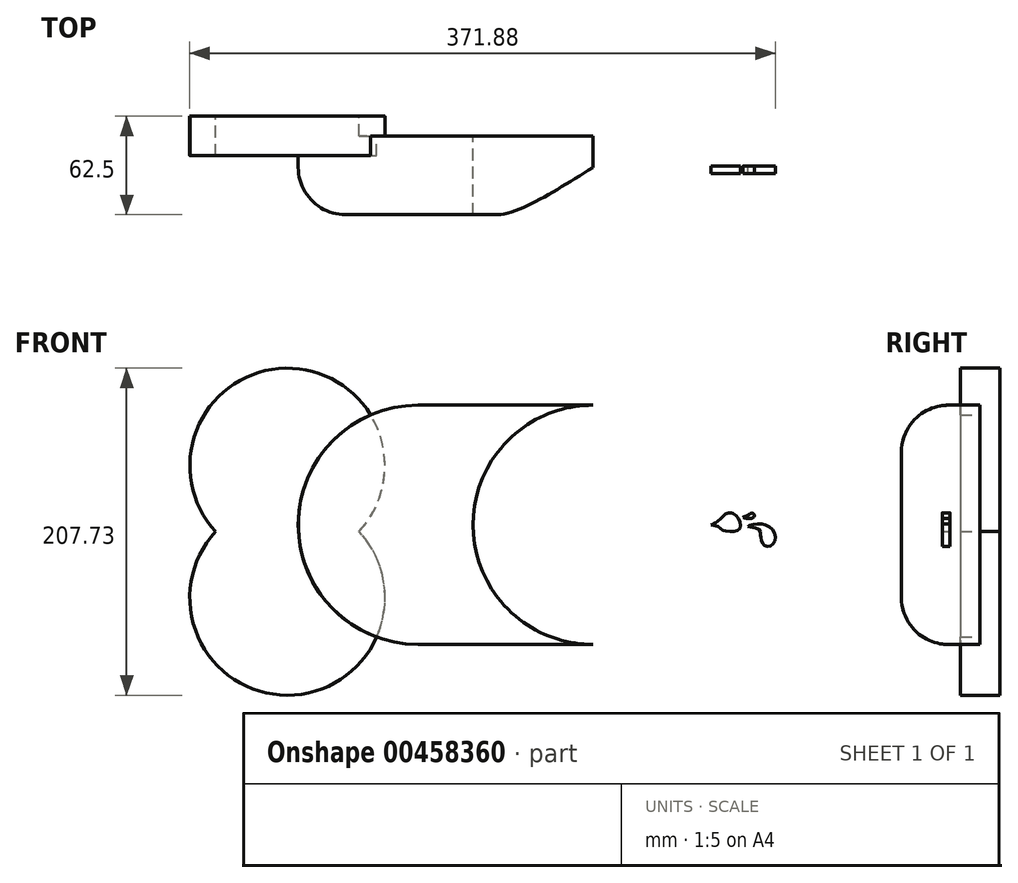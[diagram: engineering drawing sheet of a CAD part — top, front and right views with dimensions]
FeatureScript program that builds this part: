
annotation { "Feature Type Name" : "Feature", "Feature Type Description" : "" }
export const myFeature = defineFeature(function(context is Context, id is Id, definition is map)
    precondition{}
    {
        {
            var Q0;
            Q0=qCreatedBy(makeId("Front.planeOp"),FACE);
            var sketch = newSketch(context, id + "F0", { "sketchPlane" : qUnion([Q0])});
            skCircle(sketch, "E0", {"center": v(0, 0) * mm, "radius": 76 * mm});
            skCircle(sketch, "E1", {"center": v(111, 0) * mm, "radius": 76 * mm});
            skLineSegment(sketch, "E2", {"start": v(111, 76) * mm, "end": v(0, 76) * mm});
            skLineSegment(sketch, "E3", {"start": v(0, -76) * mm, "end": v(111, -76) * mm});
            skSolve(sketch);
        }
        {
            var Q0;
            Q0=qCreatedBy(makeId("Front.planeOp"),FACE);
            cPlane(context, id + "F1", {"entities" : qUnion([Q0]), "cplaneType" : CPlaneType.OFFSET, "offset" : 19 * mm, "width" : 150 * mm, "height" : 150 * mm});
        }
        {
            var Q0;
            {var subQ0=sQuery(id+"F0.wireOp",EDGE,"E0");var subQ1=makeQuery(id+"F0.imprint","INTERSECT",VERTEX,{"derivedFrom":[subQ0,sQuery(id+"F0.wireOp",EDGE,"E2")]});Q0=makeQuery(id+"F0.imprint","IMPRINT",FACE,{"disambiguationData":[TD([[makeQuery(id+"F0.imprint","IMPRINT",EDGE,{"disambiguationData":[TD([[subQ1,1.0]])],"derivedFrom":subQ0}),1.0]])]});}
            var Q1;
            {var subQ0=sQuery(id+"F0.wireOp",EDGE,"E1");var subQ1=sQuery(id+"F0.wireOp",EDGE,"E0");var subQ2=makeQuery(id+"F0.imprint","INTERSECT",VERTEX,{"disambiguationData":[OD(0.0)],"derivedFrom":[subQ1,subQ0]});Q1=makeQuery(id+"F0.imprint","IMPRINT",FACE,{"disambiguationData":[TD([[makeQuery(id+"F0.imprint","IMPRINT",EDGE,{"disambiguationData":[TD([[subQ2,1.0]])],"derivedFrom":subQ1}),-1.0]])]});}
            var Q2;
            {var subQ0=sQuery(id+"F0.wireOp",EDGE,"E1");var subQ1=sQuery(id+"F0.wireOp",EDGE,"E0");var subQ2=makeQuery(id+"F0.imprint","INTERSECT",VERTEX,{"disambiguationData":[OD(0.0)],"derivedFrom":[subQ1,subQ0]});Q2=makeQuery(id+"F0.imprint","IMPRINT",FACE,{"disambiguationData":[TD([[makeQuery(id+"F0.imprint","IMPRINT",EDGE,{"disambiguationData":[TD([[subQ2,1.0]])],"derivedFrom":subQ1}),1.0]])]});}
            var Q3;
            {var subQ0=sQuery(id+"F0.wireOp",EDGE,"E3");Q3=makeQuery(id+"F0.imprint","IMPRINT",FACE,{"disambiguationData":[TD([[makeQuery(id+"F0.imprint","IMPRINT",EDGE,{"derivedFrom":subQ0}),1.0]])]});}
            var Q4;
            {var subQ0=sQuery(id+"F0.wireOp",EDGE,"E2");Q4=makeQuery(id+"F0.imprint","IMPRINT",FACE,{"disambiguationData":[TD([[makeQuery(id+"F0.imprint","IMPRINT",EDGE,{"derivedFrom":subQ0}),1.0]])]});}
            extrude(context, id + "F2", {"entities" : qUnion([Q0, Q1, Q2, Q3, Q4]), "depth" : 50 * mm, "offsetDistance" : 25 * mm});
        }
        {
            var Q0;
            Q0=qCreatedBy(makeId("Front.planeOp"),FACE);
            var sketch = newSketch(context, id + "F3", { "sketchPlane" : qUnion([Q0])});
            skCircle(sketch, "E4", {"center": v(-82.93, 37.57) * mm, "radius": 61.92 * mm});
            skCircle(sketch, "E5", {"center": v(-82.93, -46.23) * mm, "radius": 62 * mm});
            skSolve(sketch);
        }
        {
            var Q0;
            Q0 = qSketchRegion(id + "F3", true);
            extrude(context, id + "F4", {"entities" : qUnion([Q0]), "operationType" : NewBodyOperationType.ADD, "depth" : 25 * mm, "offsetDistance" : 25 * mm, "symmetric" : true});
        }
        {
            var Q0;
            Q0=makeQuery(id+"F2.opExtrude","CAP_EDGE",EDGE,{"disambiguationData":[OSD([sQuery(id+"F0.wireOp",EDGE,"E0")])],"isStart":false});
            fillet(context, id + "F5", {"entities" : qUnion([Q0]), "radius" : 30 * mm, "tangentPropagation" : true, "allowEdgeOverflow" : false});
        }
        {
            var Q0;
            Q0=makeQuery(id+"F2.opExtrude","CAP_FACE",FACE,{"disambiguationData":[OSD([sQuery(id+"F0.wireOp",EDGE,"E0"),sQuery(id+"F0.wireOp",EDGE,"E1"),sQuery(id+"F0.wireOp",EDGE,"E2"),sQuery(id+"F0.wireOp",EDGE,"E3")])],"isStart":false});
            var sketch = newSketch(context, id + "F6", { "sketchPlane" : qUnion([Q0])});
            skLineSegment(sketch, "E6.bottom", {"start": v(187.67, -0.36) * mm, "end": v(169.29, -0.36) * mm});
            skLineSegment(sketch, "E6.top", {"start": v(187.67, 0.36) * mm, "end": v(169.29, 0.36) * mm});
            skLineSegment(sketch, "E6.left", {"start": v(187.67, -0.36) * mm, "end": v(187.67, 0.36) * mm});
            skLineSegment(sketch, "E6.right", {"start": v(169.29, -0.36) * mm, "end": v(169.29, 0.36) * mm});
            skPoint(sketch, "E6.middle", {"position": v(178.48, 0) * mm});
            skPoint(sketch, "E6.middle.positionSnap0", {"position": v(157, 0) * mm});
            skPoint(sketch, "E6.centerSnap0", {"position": v(157, 0) * mm});
            skSolve(sketch);
        }
        {
            var Q0;
            Q0 = qSketchRegion(id + "F6", true);
            extrude(context, id + "F7", {"entities" : qUnion([Q0]), "operationType" : NewBodyOperationType.REMOVE, "endBound" : BoundingType.THROUGH_ALL, "oppositeDirection" : true, "depth" : 25 * mm, "offsetDistance" : 25 * mm});
        }
        {
            var Q0;
            Q0=qCreatedBy(id+"F1.planeOp",FACE);
            var sketch = newSketch(context, id + "F8", { "sketchPlane" : qUnion([Q0])});
            skFitSpline(sketch, "E7", {"points": [v(186.24, 0) * mm, v(187.8, 0.43) * mm, v(189.84, 2.04) * mm, v(193, 4.3) * mm, v(195.65, 7.27) * mm, v(199.16, 7.5) * mm, v(199.48, 7.34) * mm, v(202.19, 5.7) * mm, v(204.6, 1.1) * mm, v(204.5, -2.17) * mm, v(201.72, -4.07) * mm, v(196.13, -4.1) * mm, v(193.03, -3.17) * mm, v(190.25, -0.88) * mm, v(186.24, 0) * mm]});
            skFitSpline(sketch, "E8", {"points": [v(209.6, -1.15) * mm, v(213.6, 0.4) * mm, v(220.46, 0) * mm, v(225.93, -4.06) * mm, v(226.45, -10.8) * mm, v(223.05, -13.73) * mm, v(219.27, -12.22) * mm, v(217.87, -8.84) * mm, v(217.6, -5.83) * mm, v(216, -2.37) * mm, v(209.6, -1.15) * mm]});
            skFitSpline(sketch, "E9", {"points": [v(206.51, 4.81) * mm, v(209, 5.69) * mm, v(210.71, 7) * mm, v(212.35, 7.35) * mm, v(213.62, 6.19) * mm, v(212.56, 4.4) * mm, v(209, 4.02) * mm, v(206.51, 4.81) * mm]});
            skSolve(sketch);
        }
        {
            var Q0;
            Q0 = qSketchRegion(id + "F8", true);
            extrude(context, id + "F9", {"entities" : qUnion([Q0]), "depth" : 5 * mm, "offsetDistance" : 25 * mm});
        }
    });
